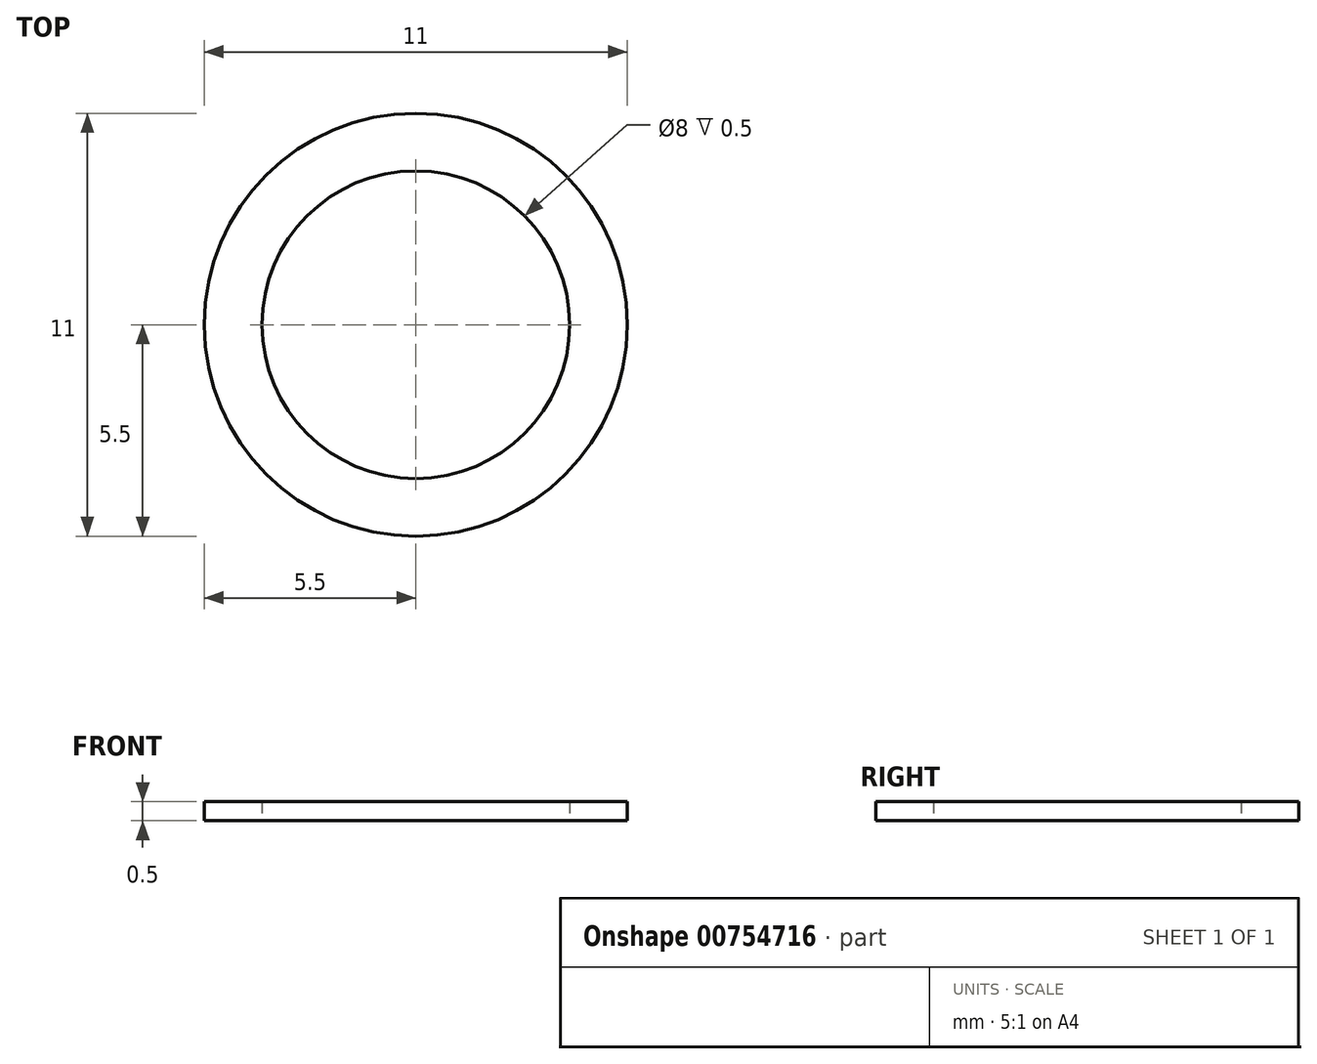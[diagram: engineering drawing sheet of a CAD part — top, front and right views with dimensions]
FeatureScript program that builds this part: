
annotation { "Feature Type Name" : "Feature", "Feature Type Description" : "" }
export const myFeature = defineFeature(function(context is Context, id is Id, definition is map)
    precondition{}
    {
        {
            var Q0;
            Q0=qCreatedBy(makeId("Top.planeOp"),FACE);
            var sketch = newSketch(context, id + "F0", { "sketchPlane" : qUnion([Q0])});
            skCircle(sketch, "E0", {"center": v(0, 0) * mm, "radius": 4 * mm});
            skCircle(sketch, "E1", {"center": v(0, 0) * mm, "radius": 5.5 * mm});
            skSolve(sketch);
        }
        {
            var Q0;
            Q0=makeQuery(id+"F0.imprint","IMPRINT",FACE,{"disambiguationData":[TD([[makeQuery(id+"F0.imprint","IMPRINT",EDGE,{"derivedFrom":sQuery(id+"F0.wireOp",EDGE,"E0")}),-1.0]])]});
            extrude(context, id + "F1", {"entities" : qUnion([Q0]), "depth" : 0.5 * mm, "offsetDistance" : 25.4 * mm});
        }
    });
